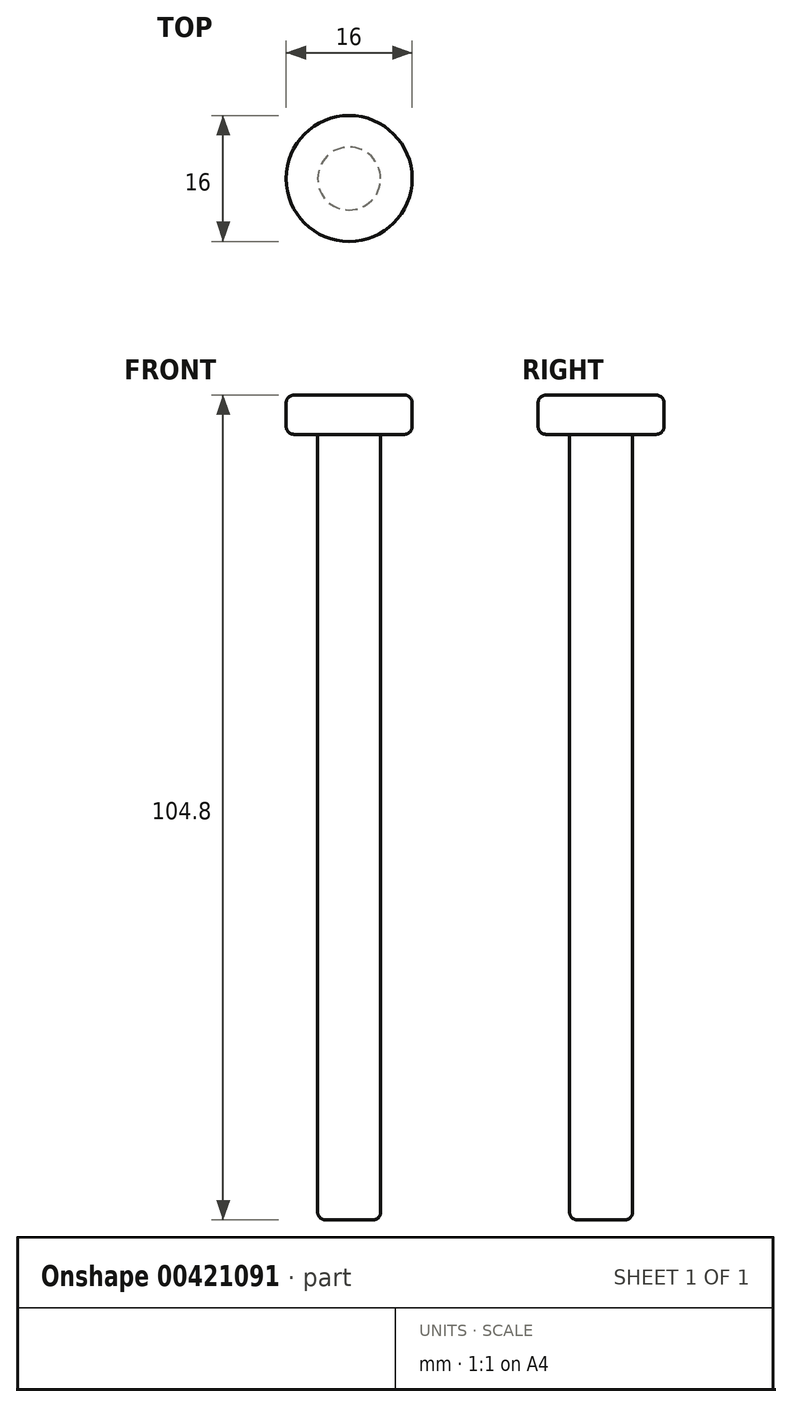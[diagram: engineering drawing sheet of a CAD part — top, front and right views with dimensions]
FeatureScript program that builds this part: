
annotation { "Feature Type Name" : "Feature", "Feature Type Description" : "" }
export const myFeature = defineFeature(function(context is Context, id is Id, definition is map)
    precondition{}
    {
        {
            var Q0;
            Q0=qCreatedBy(makeId("Top.planeOp"),FACE);
            var sketch = newSketch(context, id + "F0", { "sketchPlane" : qUnion([Q0])});
            skCircle(sketch, "E0", {"center": v(0, 0) * mm, "radius": 8 * mm});
            skSolve(sketch);
        }
        {
            var Q0;
            Q0=makeQuery(id+"F0.imprint","IMPRINT",FACE,{"disambiguationData":[TD([[makeQuery(id+"F0.imprint","IMPRINT",EDGE,{"derivedFrom":sQuery(id+"F0.wireOp",EDGE,"E0")}),1.0]])]});
            extrude(context, id + "F1", {"entities" : qUnion([Q0]), "depth" : 5 * mm});
        }
        {
            var Q0;
            Q0=makeQuery(id+"F1.opExtrude","CAP_FACE",FACE,{"disambiguationData":[OSD([sQuery(id+"F0.wireOp",EDGE,"E0")])],"isStart":true});
            var sketch = newSketch(context, id + "F2", { "sketchPlane" : qUnion([Q0])});
            skCircle(sketch, "E1", {"center": v(0, 0) * mm, "radius": 4 * mm});
            skSolve(sketch);
        }
        {
            var Q0;
            Q0 = qSketchRegion(id + "F2", true);
            var Q1;
            Q1=makeQuery(id+"F2.imprint","IMPRINT",FACE,{"disambiguationData":[TD([[makeQuery(id+"F2.imprint","IMPRINT",EDGE,{"derivedFrom":sQuery(id+"F2.wireOp",EDGE,"E1")}),1.0]])]});
            extrude(context, id + "F3", {"entities" : qUnion([Q0, Q1]), "operationType" : NewBodyOperationType.ADD, "depth" : 99.8 * mm});
        }
        {
            var Q0;
            Q0=makeQuery(id+"F3.opExtrude","CAP_EDGE",EDGE,{"disambiguationData":[OSD([sQuery(id+"F2.wireOp",EDGE,"E1")])],"isStart":false});
            var Q1;
            Q1=makeQuery(id+"F1.opExtrude","CAP_EDGE",EDGE,{"disambiguationData":[OSD([sQuery(id+"F0.wireOp",EDGE,"E0")])],"isStart":true});
            var Q2;
            Q2=makeQuery(id+"F1.opExtrude","CAP_EDGE",EDGE,{"disambiguationData":[OSD([sQuery(id+"F0.wireOp",EDGE,"E0")])],"isStart":false});
            fillet(context, id + "F4", {"entities" : qUnion([Q0, Q1, Q2]), "radius" : 1 * mm, "tangentPropagation" : true, "allowEdgeOverflow" : false});
        }
    });
